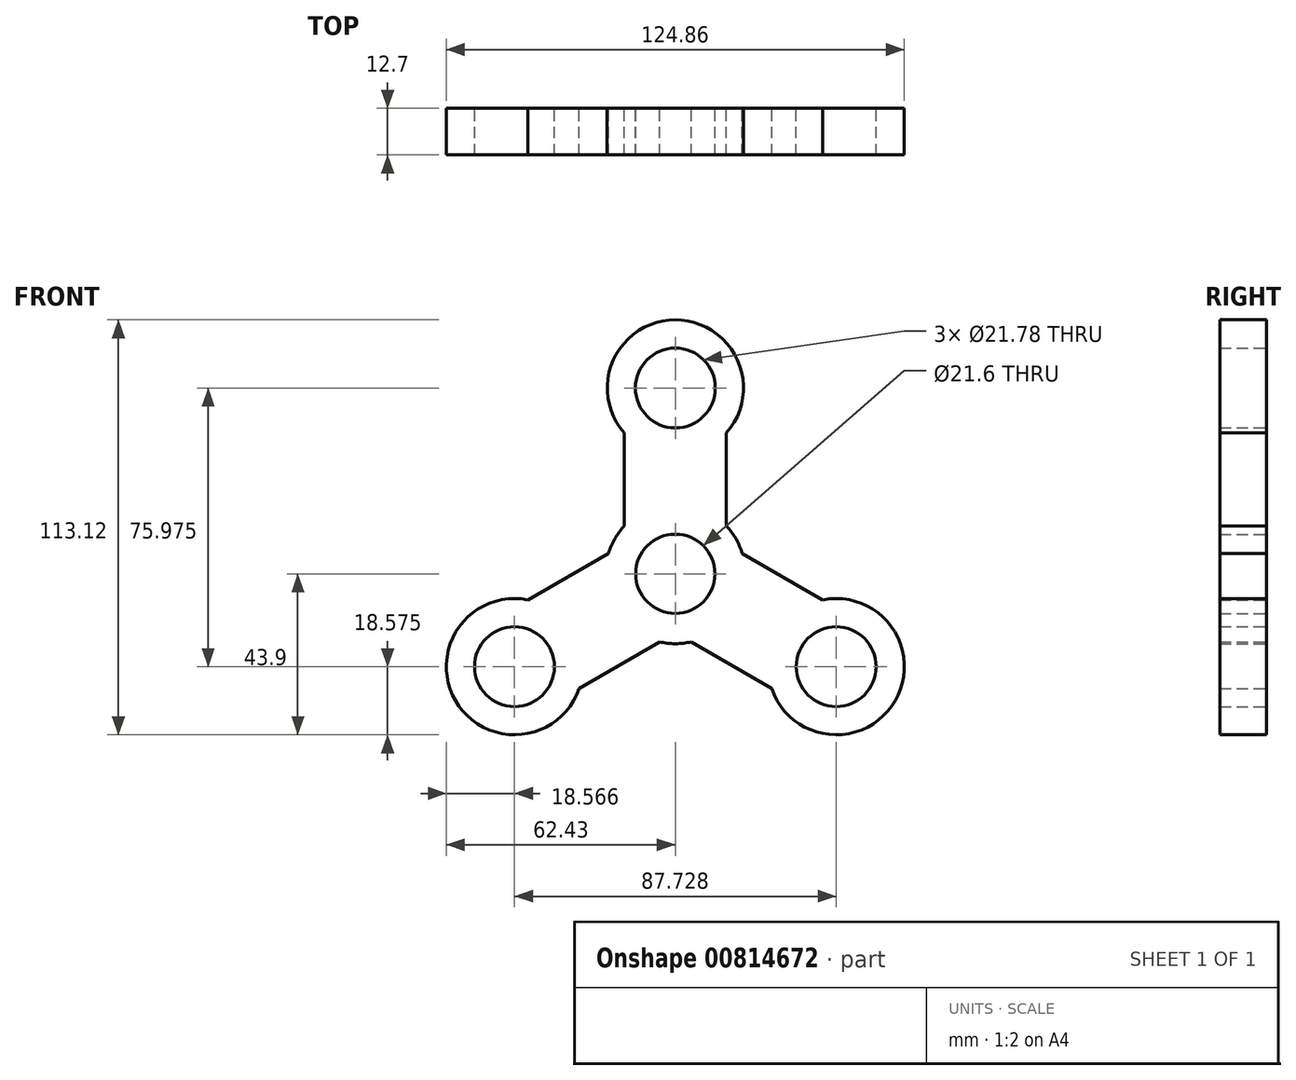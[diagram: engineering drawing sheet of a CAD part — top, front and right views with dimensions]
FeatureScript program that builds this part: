
annotation { "Feature Type Name" : "Feature", "Feature Type Description" : "" }
export const myFeature = defineFeature(function(context is Context, id is Id, definition is map)
    precondition{}
    {
        {
            var Q0;
            Q0=qCreatedBy(makeId("Front.planeOp"),FACE);
            var sketch = newSketch(context, id + "F0", { "sketchPlane" : qUnion([Q0])});
            skCircle(sketch, "E0", {"center": v(0, 0) * mm, "radius": 10.8 * mm});
            skCircle(sketch, "E1", {"center": v(0, 50.65) * mm, "radius": 10.9 * mm});
            skCircle(sketch, "E2", {"center": v(0, 50.65) * mm, "radius": 18.57 * mm});
            skCircle(sketch, "E3", {"center": v(0, 0) * mm, "radius": 19.07 * mm});
            skLineSegment(sketch, "E4", {"start": v(-13.93, 38.37) * mm, "end": v(-13.93, 13.03) * mm});
            skLineSegment(sketch, "E5", {"start": v(13.93, 38.37) * mm, "end": v(13.93, 13.03) * mm});
            skCircle(sketch, "E6.1.0", {"center": v(-43.86, -25.32) * mm, "radius": 18.57 * mm});
            skLineSegment(sketch, "E6.1.2", {"start": v(-40.2, -7.12) * mm, "end": v(-18.25, 5.55) * mm});
            skLineSegment(sketch, "E6.1.4", {"start": v(-26.26, -31.25) * mm, "end": v(-4.32, -18.58) * mm});
            skCircle(sketch, "E6.1.5", {"center": v(-43.86, -25.32) * mm, "radius": 10.9 * mm});
            skCircle(sketch, "E6.2.0", {"center": v(43.86, -25.32) * mm, "radius": 18.57 * mm});
            skLineSegment(sketch, "E6.2.2", {"start": v(26.26, -31.25) * mm, "end": v(4.32, -18.58) * mm});
            skLineSegment(sketch, "E6.2.4", {"start": v(40.2, -7.12) * mm, "end": v(18.25, 5.55) * mm});
            skCircle(sketch, "E6.2.5", {"center": v(43.86, -25.32) * mm, "radius": 10.9 * mm});
            skSolve(sketch);
        }
        {
            var Q0;
            Q0=makeQuery(id+"F0.imprint","IMPRINT",FACE,{"disambiguationData":[TD([[makeQuery(id+"F0.imprint","IMPRINT",EDGE,{"derivedFrom":sQuery(id+"F0.wireOp",EDGE,"E1")}),-1.0]])]});
            var Q1;
            {var subQ0=sQuery(id+"F0.wireOp",EDGE,"E4");Q1=makeQuery(id+"F0.imprint","IMPRINT",FACE,{"disambiguationData":[TD([[makeQuery(id+"F0.imprint","IMPRINT",EDGE,{"derivedFrom":subQ0}),1.0]])]});}
            var Q2;
            {var subQ0=sQuery(id+"F0.wireOp",EDGE,"E6.1.2");Q2=makeQuery(id+"F0.imprint","IMPRINT",FACE,{"disambiguationData":[TD([[makeQuery(id+"F0.imprint","IMPRINT",EDGE,{"derivedFrom":subQ0}),-1.0]])]});}
            var Q3;
            Q3=makeQuery(id+"F0.imprint","IMPRINT",FACE,{"disambiguationData":[TD([[makeQuery(id+"F0.imprint","IMPRINT",EDGE,{"derivedFrom":sQuery(id+"F0.wireOp",EDGE,"E0")}),-1.0]])]});
            var Q4;
            Q4=makeQuery(id+"F0.imprint","IMPRINT",FACE,{"disambiguationData":[TD([[makeQuery(id+"F0.imprint","IMPRINT",EDGE,{"derivedFrom":sQuery(id+"F0.wireOp",EDGE,"E6.1.5")}),-1.0]])]});
            var Q5;
            {var subQ0=sQuery(id+"F0.wireOp",EDGE,"E6.2.2");Q5=makeQuery(id+"F0.imprint","IMPRINT",FACE,{"disambiguationData":[TD([[makeQuery(id+"F0.imprint","IMPRINT",EDGE,{"derivedFrom":subQ0}),-1.0]])]});}
            var Q6;
            Q6=makeQuery(id+"F0.imprint","IMPRINT",FACE,{"disambiguationData":[TD([[makeQuery(id+"F0.imprint","IMPRINT",EDGE,{"derivedFrom":sQuery(id+"F0.wireOp",EDGE,"E6.2.5")}),-1.0]])]});
            extrude(context, id + "F1", {"entities" : qUnion([Q0, Q1, Q2, Q3, Q4, Q5, Q6]), "depth" : 12.7 * mm, "offsetDistance" : 25.4 * mm});
        }
    });
